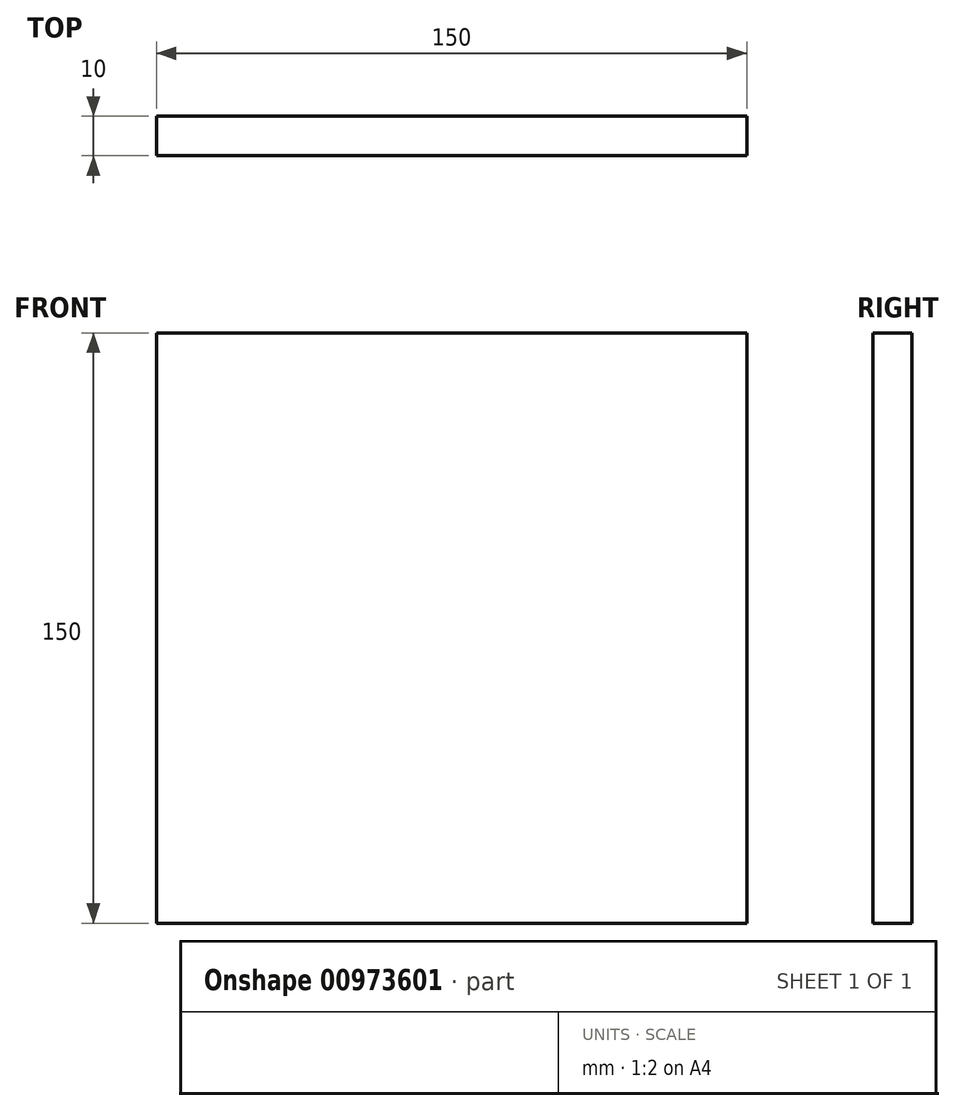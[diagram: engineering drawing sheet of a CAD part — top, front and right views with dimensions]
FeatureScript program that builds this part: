
annotation { "Feature Type Name" : "Feature", "Feature Type Description" : "" }
export const myFeature = defineFeature(function(context is Context, id is Id, definition is map)
    precondition{}
    {
        {
            var Q0;
            Q0=qCreatedBy(makeId("Front.planeOp"),FACE);
            var sketch = newSketch(context, id + "F0", { "sketchPlane" : qUnion([Q0])});
            skLineSegment(sketch, "E0.bottom", {"start": v(-150, 150) * mm, "end": v(0, 150) * mm});
            skLineSegment(sketch, "E0.top", {"start": v(-150, 0) * mm, "end": v(0, 0) * mm});
            skLineSegment(sketch, "E0.left", {"start": v(-150, 150) * mm, "end": v(-150, 0) * mm});
            skLineSegment(sketch, "E0.right", {"start": v(0, 150) * mm, "end": v(0, 0) * mm});
            skSolve(sketch);
        }
        {
            var Q0;
            Q0=makeQuery(id+"F0.imprint","IMPRINT",FACE,{"disambiguationData":[TD([[makeQuery(id+"F0.imprint","IMPRINT",EDGE,{"derivedFrom":sQuery(id+"F0.wireOp",EDGE,"E0.bottom")}),-1.0]])]});
            extrude(context, id + "F1", {"entities" : qUnion([Q0]), "depth" : 10 * mm, "offsetDistance" : 25 * mm});
        }
    });
